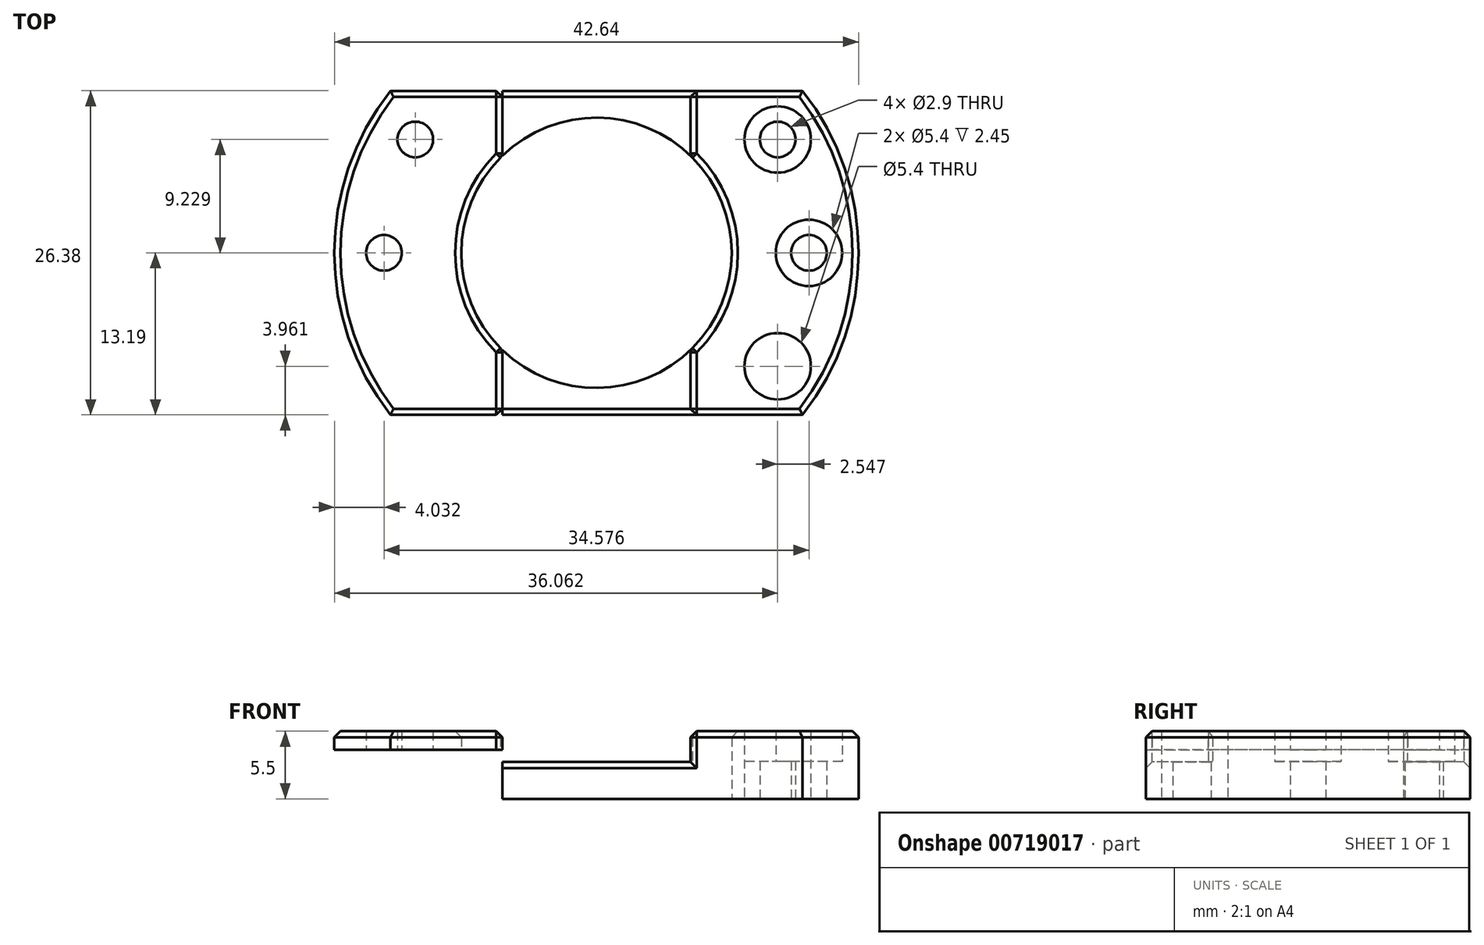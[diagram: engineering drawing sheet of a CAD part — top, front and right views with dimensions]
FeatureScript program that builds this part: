
annotation { "Feature Type Name" : "Feature", "Feature Type Description" : "" }
export const myFeature = defineFeature(function(context is Context, id is Id, definition is map)
    precondition{}
    {
        {
            var Q0;
            Q0=qCreatedBy(makeId("Top.planeOp"),FACE);
            var sketch = newSketch(context, id + "F0", { "sketchPlane" : qUnion([Q0])});
            skCircle(sketch, "E0", {"center": v(0, 0) * mm, "radius": 11 * mm});
            skArc(sketch, "E1", {"start": v(-16.76, 13.19) * mm, "mid": v(-21.32, 0) * mm, "end": v(-16.76, -13.19) * mm});
            skLineSegment(sketch, "E2.top", {"start": v(-16.76, 13.19) * mm, "end": v(16.76, 13.19) * mm});
            skLineSegment(sketch, "E3.MirrorCS", {"start": v(-16.76, -13.19) * mm, "end": v(16.76, -13.19) * mm});
            skArc(sketch, "E4.trimOffspring", {"start": v(16.76, -13.19) * mm, "mid": v(21.32, 0) * mm, "end": v(16.76, 13.19) * mm});
            skLineSegment(sketch, "E5.left", {"start": v(-7.65, -13.19) * mm, "end": v(-7.65, -7.9) * mm});
            skLineSegment(sketch, "E5.right", {"start": v(7.65, -13.19) * mm, "end": v(7.65, -7.9) * mm});
            skLineSegment(sketch, "E6.trimOffspring", {"start": v(-7.65, 7.9) * mm, "end": v(-7.65, 13.19) * mm});
            skLineSegment(sketch, "E7.trimOffspring", {"start": v(7.65, 7.9) * mm, "end": v(7.65, 13.19) * mm});
            skCircle(sketch, "E8", {"center": v(14.74, 9.23) * mm, "radius": 2.7 * mm});
            skCircle(sketch, "E9.MirrorC", {"center": v(14.74, -9.23) * mm, "radius": 2.7 * mm});
            skCircle(sketch, "E10", {"center": v(17.29, 0) * mm, "radius": 2.7 * mm});
            skCircle(sketch, "E11", {"center": v(14.74, 9.23) * mm, "radius": 1.45 * mm});
            skCircle(sketch, "E12.MirrorC", {"center": v(14.74, -9.23) * mm, "radius": 1.45 * mm});
            skCircle(sketch, "E13", {"center": v(17.29, 0) * mm, "radius": 1.45 * mm});
            skCircle(sketch, "E14.MirrorC", {"center": v(-14.74, 9.23) * mm, "radius": 1.45 * mm});
            skCircle(sketch, "E15.MirrorC", {"center": v(-17.29, 0) * mm, "radius": 1.45 * mm});
            skCircle(sketch, "E16.MirrorC", {"center": v(-14.74, -9.23) * mm, "radius": 1.45 * mm});
            skSolve(sketch);
        }
        {
            var Q0;
            {var subQ0=sQuery(id+"F0.wireOp",EDGE,"E4.trimOffspring");Q0=makeQuery(id+"F0.imprint","IMPRINT",FACE,{"disambiguationData":[TD([[makeQuery(id+"F0.imprint","IMPRINT",EDGE,{"derivedFrom":subQ0}),1.0]])]});}
            var Q1;
            {var subQ0=sQuery(id+"F0.wireOp",EDGE,"E6.trimOffspring");Q1=makeQuery(id+"F0.imprint","IMPRINT",FACE,{"disambiguationData":[TD([[makeQuery(id+"F0.imprint","IMPRINT",EDGE,{"derivedFrom":subQ0}),-1.0]])]});}
            var Q2;
            {var subQ1=sQuery(id+"F0.wireOp",EDGE,"E1");Q2=makeQuery(id+"F0.imprint","IMPRINT",FACE,{"disambiguationData":[TD([[makeQuery(id+"F0.imprint","IMPRINT",EDGE,{"derivedFrom":subQ1}),1.0]])]});}
            var Q3;
            {var subQ0=sQuery(id+"F0.wireOp",EDGE,"E5.left");Q3=makeQuery(id+"F0.imprint","IMPRINT",FACE,{"disambiguationData":[TD([[makeQuery(id+"F0.imprint","IMPRINT",EDGE,{"derivedFrom":subQ0}),-1.0]])]});}
            extrude(context, id + "F1", {"entities" : qUnion([Q0, Q1, Q2, Q3]), "depth" : 3 * mm, "offsetDistance" : 25 * mm});
        }
        {
            var Q0;
            {var subQ1=sQuery(id+"F0.wireOp",EDGE,"E1");Q0=makeQuery(id+"F0.imprint","IMPRINT",FACE,{"disambiguationData":[TD([[makeQuery(id+"F0.imprint","IMPRINT",EDGE,{"derivedFrom":subQ1}),1.0]])]});}
            var Q1;
            {var subQ0=sQuery(id+"F0.wireOp",EDGE,"E4.trimOffspring");Q1=makeQuery(id+"F0.imprint","IMPRINT",FACE,{"disambiguationData":[TD([[makeQuery(id+"F0.imprint","IMPRINT",EDGE,{"derivedFrom":subQ0}),1.0]])]});}
            var Q2;
            Q2=makeQuery(id+"F0.imprint","IMPRINT",FACE,{"disambiguationData":[TD([[makeQuery(id+"F0.imprint","IMPRINT",EDGE,{"derivedFrom":sQuery(id+"F0.wireOp",EDGE,"E14.MirrorC")}),-1.0]])]});
            var Q3;
            Q3=makeQuery(id+"F0.imprint","IMPRINT",FACE,{"disambiguationData":[TD([[makeQuery(id+"F0.imprint","IMPRINT",EDGE,{"derivedFrom":sQuery(id+"F0.wireOp",EDGE,"E15.MirrorC")}),-1.0]])]});
            var Q4;
            Q4=makeQuery(id+"F0.imprint","IMPRINT",FACE,{"disambiguationData":[TD([[makeQuery(id+"F0.imprint","IMPRINT",EDGE,{"derivedFrom":sQuery(id+"F0.wireOp",EDGE,"E16.MirrorC")}),1.0]])]});
            extrude(context, id + "F2", {"entities" : qUnion([Q0, Q1, Q2, Q3, Q4]), "operationType" : NewBodyOperationType.ADD, "depth" : 5.5 * mm, "offsetDistance" : 25 * mm});
        }
        {
            var Q0;
            Q0=makeQuery(id+"F0.imprint","IMPRINT",FACE,{"disambiguationData":[TD([[makeQuery(id+"F0.imprint","IMPRINT",EDGE,{"derivedFrom":sQuery(id+"F0.wireOp",EDGE,"E8")}),1.0]])]});
            var Q1;
            Q1=makeQuery(id+"F0.imprint","IMPRINT",FACE,{"disambiguationData":[TD([[makeQuery(id+"F0.imprint","IMPRINT",EDGE,{"derivedFrom":sQuery(id+"F0.wireOp",EDGE,"E10")}),1.0]])]});
            var Q2;
            Q2=makeQuery(id+"F0.imprint","IMPRINT",FACE,{"disambiguationData":[TD([[makeQuery(id+"F0.imprint","IMPRINT",EDGE,{"derivedFrom":sQuery(id+"F0.wireOp",EDGE,"E9.MirrorC")}),-1.0]])]});
            extrude(context, id + "F3", {"entities" : qUnion([Q0, Q1, Q2]), "operationType" : NewBodyOperationType.ADD, "depth" : 3.05 * mm, "offsetDistance" : 25 * mm});
        }
        {
            var Q0;
            Q0=makeQuery(id+"F0.imprint","IMPRINT",FACE,{"disambiguationData":[TD([[makeQuery(id+"F0.imprint","IMPRINT",EDGE,{"derivedFrom":sQuery(id+"F0.wireOp",EDGE,"E14.MirrorC")}),-1.0]])]});
            var Q1;
            Q1=makeQuery(id+"F0.imprint","IMPRINT",FACE,{"disambiguationData":[TD([[makeQuery(id+"F0.imprint","IMPRINT",EDGE,{"derivedFrom":sQuery(id+"F0.wireOp",EDGE,"E15.MirrorC")}),-1.0]])]});
            var Q2;
            Q2=makeQuery(id+"F0.imprint","IMPRINT",FACE,{"disambiguationData":[TD([[makeQuery(id+"F0.imprint","IMPRINT",EDGE,{"derivedFrom":sQuery(id+"F0.wireOp",EDGE,"E16.MirrorC")}),1.0]])]});
            extrude(context, id + "F4", {"entities" : qUnion([Q0, Q1, Q2]), "operationType" : NewBodyOperationType.REMOVE, "depth" : 4 * mm, "offsetDistance" : 25 * mm});
        }
        {
            var Q0;
            Q0=makeQuery(id+"F2.opExtrude","CAP_EDGE",EDGE,{"disambiguationData":[OSD([sQuery(id+"F0.wireOp",EDGE,"E1")])],"isStart":false});
            var Q1;
            {var subQ0=sQuery(id+"F0.wireOp",EDGE,"E3.MirrorCS");Q1=makeQuery(id+"F2.opExtrude","CAP_EDGE",EDGE,{"disambiguationData":[OSD([subQ0]),TDD([makeQuery(id+"F0.imprint","IMPRINT",EDGE,{"disambiguationData":[TD([[makeQuery(id+"F0.imprint","INTERSECT",VERTEX,{"derivedFrom":[sQuery(id+"F0.wireOp",EDGE,"E1"),subQ0]}),-1.0]])],"derivedFrom":subQ0})])],"isStart":false});}
            var Q2;
            Q2=makeQuery(id+"F2.opExtrude","CAP_EDGE",EDGE,{"disambiguationData":[OSD([sQuery(id+"F0.wireOp",EDGE,"E5.left")])],"isStart":false});
            var Q3;
            {var subQ0=sQuery(id+"F0.wireOp",EDGE,"E0");Q3=makeQuery(id+"F2.opExtrude","CAP_EDGE",EDGE,{"disambiguationData":[OSD([subQ0]),TDD([makeQuery(id+"F0.imprint","IMPRINT",EDGE,{"disambiguationData":[TD([[makeQuery(id+"F0.imprint","INTERSECT",VERTEX,{"derivedFrom":[subQ0,sQuery(id+"F0.wireOp",EDGE,"E5.left")]}),1.0]])],"derivedFrom":subQ0})])],"isStart":false});}
            var Q4;
            Q4=makeQuery(id+"F2.opExtrude","CAP_EDGE",EDGE,{"disambiguationData":[OSD([sQuery(id+"F0.wireOp",EDGE,"E6.trimOffspring")])],"isStart":false});
            var Q5;
            {var subQ0=sQuery(id+"F0.wireOp",EDGE,"E2.top");Q5=makeQuery(id+"F2.opExtrude","CAP_EDGE",EDGE,{"disambiguationData":[OSD([subQ0]),TDD([makeQuery(id+"F0.imprint","IMPRINT",EDGE,{"disambiguationData":[TD([[makeQuery(id+"F0.imprint","INTERSECT",VERTEX,{"derivedFrom":[sQuery(id+"F0.wireOp",EDGE,"E1"),subQ0]}),-1.0]])],"derivedFrom":subQ0})])],"isStart":false});}
            var Q6;
            Q6=makeQuery(id+"F2.opExtrude","SWEPT_EDGE",EDGE,{"disambiguationData":[OSD([sQuery(id+"F0.wireOp",EDGE,"E2.top"),sQuery(id+"F0.wireOp",EDGE,"E6.trimOffspring")])]});
            var Q7;
            Q7=makeQuery(id+"F1.opExtrude","CAP_EDGE",EDGE,{"disambiguationData":[OSD([sQuery(id+"F0.wireOp",EDGE,"E2.top")])],"isStart":false});
            var Q8;
            Q8=makeQuery(id+"F2.opExtrude","SWEPT_EDGE",EDGE,{"disambiguationData":[OSD([sQuery(id+"F0.wireOp",EDGE,"E0"),sQuery(id+"F0.wireOp",EDGE,"E6.trimOffspring")])]});
            var Q9;
            Q9=makeQuery(id+"F2.opExtrude","SWEPT_EDGE",EDGE,{"disambiguationData":[OSD([sQuery(id+"F0.wireOp",EDGE,"E3.MirrorCS"),sQuery(id+"F0.wireOp",EDGE,"E5.left")])]});
            var Q10;
            Q10=makeQuery(id+"F2.opExtrude","SWEPT_EDGE",EDGE,{"disambiguationData":[OSD([sQuery(id+"F0.wireOp",EDGE,"E0"),sQuery(id+"F0.wireOp",EDGE,"E5.left")])]});
            var Q11;
            Q11=makeQuery(id+"F2.opExtrude","SWEPT_EDGE",EDGE,{"disambiguationData":[OSD([sQuery(id+"F0.wireOp",EDGE,"E0"),sQuery(id+"F0.wireOp",EDGE,"E7.trimOffspring")])]});
            var Q12;
            Q12=makeQuery(id+"F2.opExtrude","CAP_EDGE",EDGE,{"disambiguationData":[OSD([sQuery(id+"F0.wireOp",EDGE,"E7.trimOffspring")])],"isStart":false});
            var Q13;
            Q13=makeQuery(id+"F2.opExtrude","SWEPT_EDGE",EDGE,{"disambiguationData":[OSD([sQuery(id+"F0.wireOp",EDGE,"E2.top"),sQuery(id+"F0.wireOp",EDGE,"E7.trimOffspring")])]});
            var Q14;
            Q14=makeQuery(id+"F2.opExtrude","SWEPT_EDGE",EDGE,{"disambiguationData":[OSD([sQuery(id+"F0.wireOp",EDGE,"E0"),sQuery(id+"F0.wireOp",EDGE,"E5.right")])]});
            var Q15;
            Q15=makeQuery(id+"F2.opExtrude","SWEPT_EDGE",EDGE,{"disambiguationData":[OSD([sQuery(id+"F0.wireOp",EDGE,"E3.MirrorCS"),sQuery(id+"F0.wireOp",EDGE,"E5.right")])]});
            var Q16;
            {var subQ0=sQuery(id+"F0.wireOp",EDGE,"E3.MirrorCS");Q16=makeQuery(id+"F2.opExtrude","CAP_EDGE",EDGE,{"disambiguationData":[OSD([subQ0]),TDD([makeQuery(id+"F0.imprint","IMPRINT",EDGE,{"disambiguationData":[TD([[makeQuery(id+"F0.imprint","INTERSECT",VERTEX,{"derivedFrom":[subQ0,sQuery(id+"F0.wireOp",EDGE,"E4.trimOffspring")]}),1.0]])],"derivedFrom":subQ0})])],"isStart":false});}
            var Q17;
            {var subQ0=sQuery(id+"F0.wireOp",EDGE,"E2.top");Q17=makeQuery(id+"F2.opExtrude","CAP_EDGE",EDGE,{"disambiguationData":[OSD([subQ0]),TDD([makeQuery(id+"F0.imprint","IMPRINT",EDGE,{"disambiguationData":[TD([[makeQuery(id+"F0.imprint","INTERSECT",VERTEX,{"derivedFrom":[subQ0,sQuery(id+"F0.wireOp",EDGE,"E4.trimOffspring")]}),1.0]])],"derivedFrom":subQ0})])],"isStart":false});}
            var Q18;
            Q18=makeQuery(id+"F2.opExtrude","CAP_EDGE",EDGE,{"disambiguationData":[OSD([sQuery(id+"F0.wireOp",EDGE,"E4.trimOffspring")])],"isStart":false});
            var Q19;
            Q19=makeQuery(id+"F2.opExtrude","CAP_EDGE",EDGE,{"disambiguationData":[OSD([sQuery(id+"F0.wireOp",EDGE,"E5.right")])],"isStart":false});
            var Q20;
            Q20=makeQuery(id+"F1.opExtrude","CAP_EDGE",EDGE,{"disambiguationData":[OSD([sQuery(id+"F0.wireOp",EDGE,"E3.MirrorCS")])],"isStart":false});
            var Q21;
            {var subQ0=sQuery(id+"F0.wireOp",EDGE,"E0");Q21=makeQuery(id+"F2.opExtrude","CAP_EDGE",EDGE,{"disambiguationData":[OSD([subQ0]),TDD([makeQuery(id+"F0.imprint","IMPRINT",EDGE,{"disambiguationData":[TD([[makeQuery(id+"F0.imprint","INTERSECT",VERTEX,{"derivedFrom":[subQ0,sQuery(id+"F0.wireOp",EDGE,"E5.right")]}),-1.0]])],"derivedFrom":subQ0})])],"isStart":false});}
            chamfer(context, id + "F5", {"entities" : qUnion([Q0, Q1, Q2, Q3, Q4, Q5, Q6, Q7, Q8, Q9, Q10, Q11, Q12, Q13, Q14, Q15, Q16, Q17, Q18, Q19, Q20, Q21]), "width" : .5 * mm, "tangentPropagation" : true});
        }
    });
